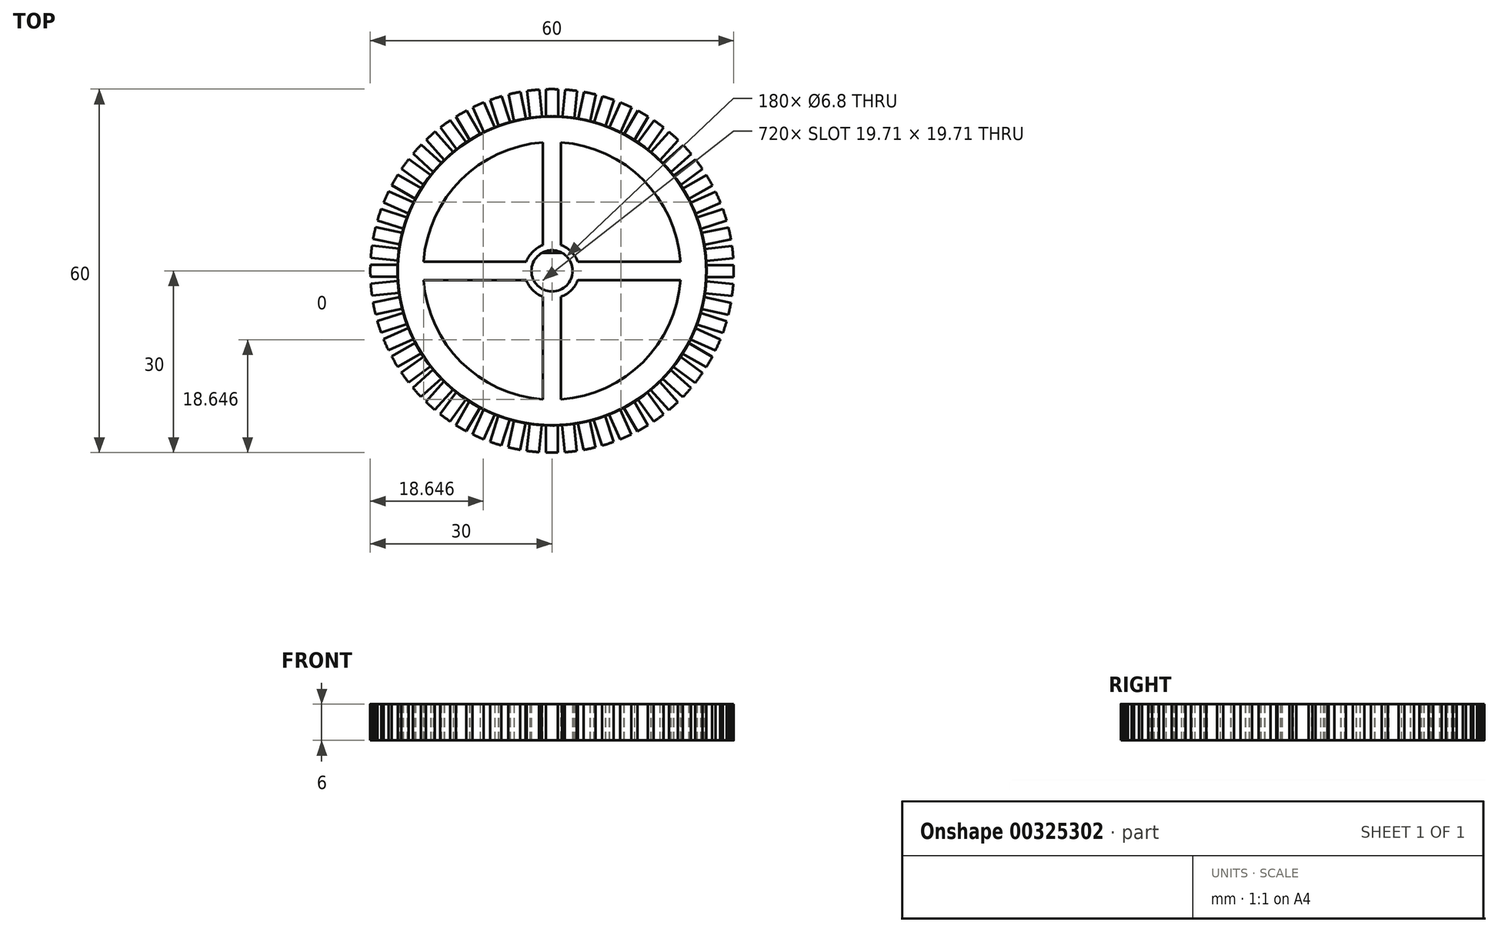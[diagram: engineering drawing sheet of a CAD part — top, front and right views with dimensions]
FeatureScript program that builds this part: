
annotation { "Feature Type Name" : "Feature", "Feature Type Description" : "" }
export const myFeature = defineFeature(function(context is Context, id is Id, definition is map)
    precondition{}
    {
        {
            var Q0;
            Q0=qCreatedBy(makeId("Top.planeOp"),FACE);
            var sketch = newSketch(context, id + "F0", { "sketchPlane" : qUnion([Q0])});
            skCircle(sketch, "E0", {"center": v(0, 0) * mm, "radius": 3.4 * mm});
            skCircle(sketch, "E1", {"center": v(0, 0) * mm, "radius": 25.5 * mm});
            skCircle(sketch, "E2", {"center": v(0, 0) * mm, "radius": 30 * mm});
            skLineSegment(sketch, "E3", {"start": v(-1.65, 2.97) * mm, "end": v(1.65, 2.97) * mm});
            skLineSegment(sketch, "E4", {"start": v(-0.97, 29.98) * mm, "end": v(-0.97, 25.48) * mm});
            skLineSegment(sketch, "E5", {"start": v(1.03, 29.98) * mm, "end": v(1.03, 25.48) * mm});
            skSolve(sketch);
        }
        {
            var Q0;
            Q0=qCreatedBy(makeId("Right.planeOp"),FACE);
            var sketch = newSketch(context, id + "F1", { "sketchPlane" : qUnion([Q0])});
            skLineSegment(sketch, "E6", {"start": v(0, 0) * mm, "end": v(0, 30.5) * mm});
            skSolve(sketch);
        }
        {
            var Q0;
            {var subQ0=sQuery(id+"F0.wireOp",EDGE,"E3");var subQ1=sQuery(id+"F0.wireOp",EDGE,"E0");var subQ2=makeQuery(id+"F0.imprint","INTERSECT",VERTEX,{"disambiguationData":[OD(0.0)],"derivedFrom":[subQ1,subQ0]});Q0=makeQuery(id+"F0.imprint","IMPRINT",FACE,{"disambiguationData":[TD([[makeQuery(id+"F0.imprint","IMPRINT",EDGE,{"disambiguationData":[TD([[subQ2,1.0]])],"derivedFrom":subQ1}),-1.0]])]});}
            var Q1;
            {var subQ0=sQuery(id+"F0.wireOp",EDGE,"I8gczHRy-Zdn1-kFwf-Mylr-sZCg1c14YUpj");Q1=makeQuery(id+"F0.imprint","IMPRINT",FACE,{"disambiguationData":[TD([[makeQuery(id+"F0.imprint","IMPRINT",EDGE,{"derivedFrom":subQ0}),1.0]])]});}
            var Q2;
            {var subQ0=sQuery(id+"F0.wireOp",EDGE,"E4");Q2=makeQuery(id+"F0.imprint","IMPRINT",FACE,{"disambiguationData":[TD([[makeQuery(id+"F0.imprint","IMPRINT",EDGE,{"derivedFrom":subQ0}),1.0]])]});}
            extrude(context, id + "F2", {"entities" : qUnion([Q0, Q1, Q2]), "depth" : 6 * mm});
        }
        {
            var Q0;
            Q0=makeQuery(id+"F2.opExtrude","SWEPT_BODY",BODY,{"disambiguationData":[OSD([sQuery(id+"F0.wireOp",EDGE,"E0"),sQuery(id+"F0.wireOp",EDGE,"E1"),sQuery(id+"F0.wireOp",EDGE,"I8gczHRy-Zdn1-kFwf-Mylr-sZCg1c14YUpj"),sQuery(id+"F0.wireOp",EDGE,"HCjG2eor-XZ6Y-jEYa-DNNx-zCT9uJ04ZVtv")])]});
            var Q1;
            Q1=sQuery(id+"F1.wireOp",EDGE,"E6");
            circularPattern(context, id + "F3", {"entities" : qUnion([Q0]), "axis" : qUnion([Q1]), "angle" : 360 * degree, "instanceCount" : 60, "equalSpace" : true});
        }
        {
            var Q0;
            {var subQ0=sQuery(id+"F0.wireOp",EDGE,"E3");Q0=makeQuery(id+"F0.imprint","IMPRINT",FACE,{"disambiguationData":[TD([[makeQuery(id+"F0.imprint","IMPRINT",EDGE,{"derivedFrom":subQ0}),1.0]])]});}
            extrude(context, id + "F4", {"entities" : qUnion([Q0]), "depth" : 6 * mm});
        }
        {
            var Q0;
            Q0=makeQuery(id+"F3.opPattern","COPY",FACE,{"derivedFrom":makeQuery(id+"F2.opExtrude","CAP_FACE",FACE,{"disambiguationData":[OSD([sQuery(id+"F0.wireOp",EDGE,"E0"),sQuery(id+"F0.wireOp",EDGE,"E1"),sQuery(id+"F0.wireOp",EDGE,"I8gczHRy-Zdn1-kFwf-Mylr-sZCg1c14YUpj"),sQuery(id+"F0.wireOp",EDGE,"HCjG2eor-XZ6Y-jEYa-DNNx-zCT9uJ04ZVtv")])],"isStart":false}),"instanceName":"30"});
            var sketch = newSketch(context, id + "F5", { "sketchPlane" : qUnion([Q0])});
            skCircle(sketch, "E7", {"center": v(0, 0) * mm, "radius": 4.5 * mm});
            skCircle(sketch, "E8", {"center": v(0, 0) * mm, "radius": 21.26 * mm});
            skLineSegment(sketch, "E9", {"start": v(-4.24, 1.5) * mm, "end": v(-4.24, -1.5) * mm});
            skLineSegment(sketch, "E10", {"start": v(-1.5, 4.24) * mm, "end": v(1.5, 4.24) * mm});
            skLineSegment(sketch, "E11", {"start": v(4.24, 1.5) * mm, "end": v(4.24, -1.5) * mm});
            skLineSegment(sketch, "E12", {"start": v(-1.5, -4.24) * mm, "end": v(1.5, -4.24) * mm});
            skLineSegment(sketch, "E13", {"start": v(-4.24, 1.5) * mm, "end": v(-21.2, 1.5) * mm});
            skLineSegment(sketch, "E14", {"start": v(-4.24, -1.5) * mm, "end": v(-21.2, -1.5) * mm});
            skLineSegment(sketch, "E15", {"start": v(-1.5, 4.24) * mm, "end": v(-1.5, 21.2) * mm});
            skLineSegment(sketch, "E16", {"start": v(1.5, 4.24) * mm, "end": v(1.5, 21.2) * mm});
            skLineSegment(sketch, "E17", {"start": v(4.24, 1.5) * mm, "end": v(21.2, 1.5) * mm});
            skLineSegment(sketch, "E18", {"start": v(4.24, -1.5) * mm, "end": v(21.2, -1.5) * mm});
            skLineSegment(sketch, "E19", {"start": v(-1.5, -4.24) * mm, "end": v(-1.5, -21.2) * mm});
            skLineSegment(sketch, "E20", {"start": v(1.5, -4.24) * mm, "end": v(1.5, -21.2) * mm});
            skSolve(sketch);
        }
        {
            var Q0;
            {var subQ0=sQuery(id+"F5.wireOp",EDGE,"E16");Q0=makeQuery(id+"F5.imprint","IMPRINT",FACE,{"disambiguationData":[TD([[makeQuery(id+"F5.imprint","IMPRINT",EDGE,{"derivedFrom":subQ0}),-1.0]])]});}
            var Q1;
            {var subQ0=sQuery(id+"F5.wireOp",EDGE,"E18");Q1=makeQuery(id+"F5.imprint","IMPRINT",FACE,{"disambiguationData":[TD([[makeQuery(id+"F5.imprint","IMPRINT",EDGE,{"derivedFrom":subQ0}),-1.0]])]});}
            var Q2;
            {var subQ0=sQuery(id+"F5.wireOp",EDGE,"E14");Q2=makeQuery(id+"F5.imprint","IMPRINT",FACE,{"disambiguationData":[TD([[makeQuery(id+"F5.imprint","IMPRINT",EDGE,{"derivedFrom":subQ0}),1.0]])]});}
            var Q3;
            {var subQ0=sQuery(id+"F5.wireOp",EDGE,"E13");Q3=makeQuery(id+"F5.imprint","IMPRINT",FACE,{"disambiguationData":[TD([[makeQuery(id+"F5.imprint","IMPRINT",EDGE,{"derivedFrom":subQ0}),-1.0]])]});}
            extrude(context, id + "F6", {"entities" : qUnion([Q0, Q1, Q2, Q3]), "operationType" : NewBodyOperationType.REMOVE, "oppositeDirection" : true, "depth" : 25 * mm});
        }
    });
